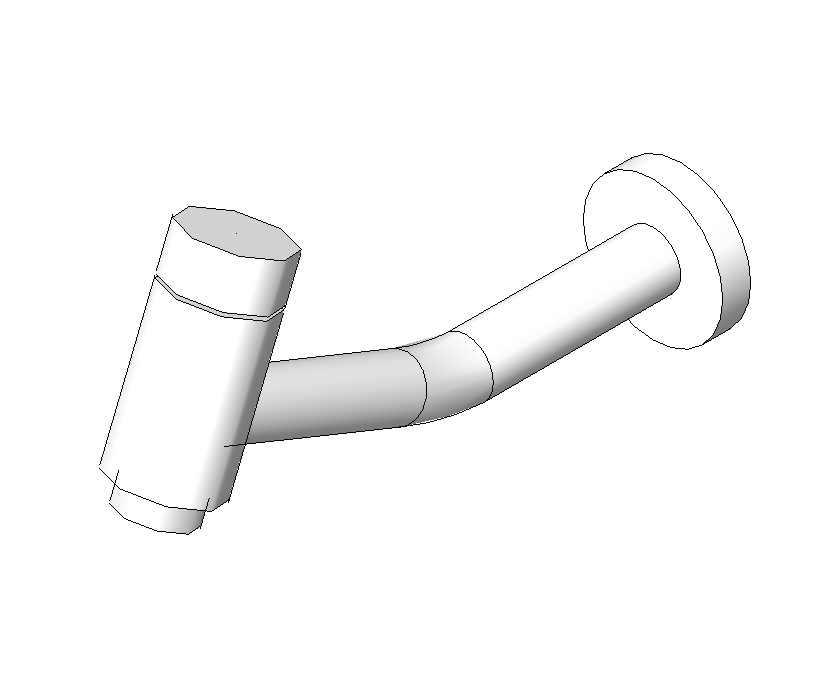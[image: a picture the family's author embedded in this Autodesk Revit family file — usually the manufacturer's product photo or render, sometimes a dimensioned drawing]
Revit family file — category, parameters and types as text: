
# Revit family: Deca_Torneira de parede para lavatório_Tube_1178.LNK
name_source: partatom
category: Plumbing Fixtures
units: mm (PartAtom-declared; Revit-internal decimal feet)

## family parameters
Cut with Voids When Loaded = No
Host = Face
Part Type = Normal
Room Calculation Point = No
Round Connector Dimension = Use Radius
Shared = No

## types (1)
- 1178.C.LNK_Cromado
    Acompanha o Produto = Acompanha Deca confort
    Aprovado por = quattroD
    Atendimento ao Cliente = 0800-0117073
    CWFU = 0
    Categoria = METAIS PARA BANHEIRO
    Composição Anel Vedação = -
    Composição Assento = -
    Composição Básica = Liga de Cobre (bronze e latão),Plásticos de Engenharia,Elastômeros
    Composição Componente = -
    Consumo = -
    Cor Interna = -
    Cor Principal = Cromado
    Cor Secundária = -
    Cores Componente = -
    Criado por = quattroD
    Código Pai = 1178.LNK
    Default Elevation = 1100 mm
    Description = Torneira de parede para lavatório
    Diâmetro Água Fria = 15 mm  [stored 0.0492126 ft]
    Informações Complementares = -
    Itens de Instalação = -
    Linha = Link
    Manufacturer = Deca
    Material = Deca_Cromado
    Model = 1178.C.LNK
    Norma = NBR10281
    Peso Líquido (Kg) = 0.578
    Pressão máx. funcionamento = 40 MCA
    Pressão mín. Aquec. Acúmulo = -
    Pressão mín. Aquec. Passagem = -
    Pressão mín. funcionamento = 2 MCA
    Raio Água Fria = 8 mm  [stored 0.0262467 ft]
    Saída de Esgoto = -
    Segmento = Banheiro Competitivo
    Tipo de dispositivo economizador = Sim
    Tipo de mecanismo utilizado = MVC -1/4 volta
    Tipo de rosca de entrada = BSP NBR 8133
    Tipo de rosca de saída = -
    URL = www.deca.com.br
    Vazão na Pressão máx. (L/min) = 6
    Vazão na Pressão mín. (L/min) = 4

note: source unit labels omitted for Vazão na Pressão máx. (L/min), Vazão na Pressão mín. (L/min) — the stored unit's dimension contradicts the parameter name (converter mislabeling)

note: [stored X ft] marks values corroborated as IEEE doubles in the binary element streams (Revit-internal decimal feet)

## geometry (parser evidence)
native form markers: Sweep x4
no freeform markers — native parametric forms only
